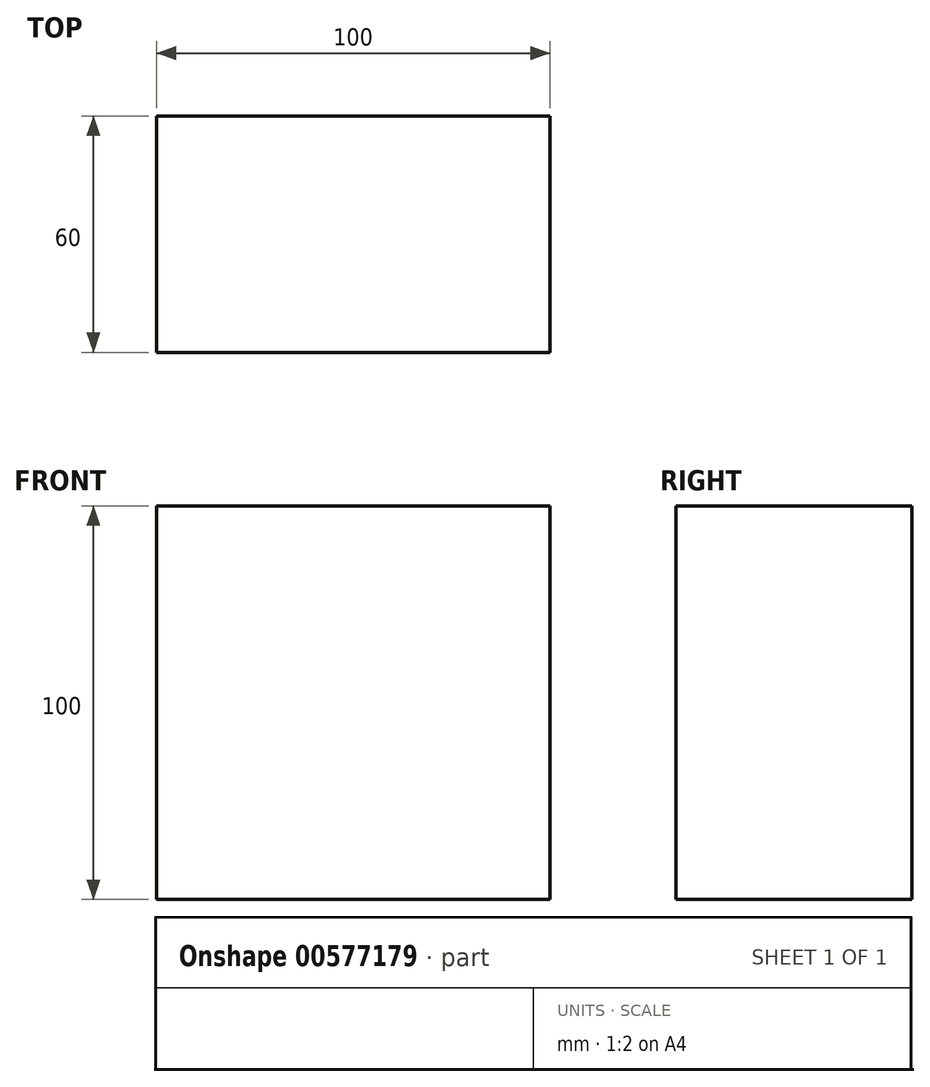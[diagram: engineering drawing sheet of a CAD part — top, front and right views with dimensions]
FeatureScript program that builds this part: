
annotation { "Feature Type Name" : "Feature", "Feature Type Description" : "" }
export const myFeature = defineFeature(function(context is Context, id is Id, definition is map)
    precondition{}
    {
        {
            var Q0;
            Q0=qCreatedBy(makeId("Front.planeOp"),FACE);
            var sketch = newSketch(context, id + "F0", { "sketchPlane" : qUnion([Q0])});
            skLineSegment(sketch, "E0.bottom", {"start": v(-50, 50) * mm, "end": v(50, 50) * mm});
            skLineSegment(sketch, "E0.top", {"start": v(-50, -50) * mm, "end": v(50, -50) * mm});
            skLineSegment(sketch, "E0.left", {"start": v(-50, 50) * mm, "end": v(-50, -50) * mm});
            skLineSegment(sketch, "E0.right", {"start": v(50, 50) * mm, "end": v(50, -50) * mm});
            skPoint(sketch, "E0.middle", {"position": v(0, 0) * mm});
            skSolve(sketch);
        }
        {
            var Q0;
            Q0=makeQuery(id+"F0.imprint","IMPRINT",FACE,{"disambiguationData":[TD([[makeQuery(id+"F0.imprint","IMPRINT",EDGE,{"derivedFrom":sQuery(id+"F0.wireOp",EDGE,"E0.bottom")}),-1.0]])]});
            extrude(context, id + "F1", {"entities" : qUnion([Q0]), "depth" : 60 * mm, "offsetDistance" : 25.4 * mm});
        }
    });
